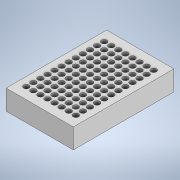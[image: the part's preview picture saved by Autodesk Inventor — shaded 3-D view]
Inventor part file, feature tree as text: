
AUTODESK INVENTOR PART (.ipt)
format: ipt  version: 2020 (Build 240168000, 168)  size: 244,736 bytes
history: native  units: in
note: dims shown in document units (in); Inventor stores cm internally (conversion verified against a paired STEP export)
features: sketch x2, extrude x1, hole x1, pattern_linear x1
ambient origin geometry x8: Origin, YZ Plane, XZ Plane, XY Plane, X Axis, Y Axis, Z Axis, Center Point
bodies: Solid1 (feature_tree)
feature tree (5):
  extrude  "Extrusion1"  Depth=5.03in
  hole  "Hole1"  [1 undecoded]
  pattern_linear  "Rectangular Pattern1"  Spacing1=0.5661in  [1 undecoded]
  sketch  "Sketch1"  dims[d0=3.365in d1=5.03in]
  sketch  "Sketch2"  dims[d2=1.0in d3=0.0in d4=0.4425in d5=0.5661in d6=0.2756in d7=0.2756in d8=0.75in d9=0.37in d10=0.25in d11=90.0deg d12=0.75in d13=0.0in d14=3.1496in d16=0.3543in d17=4.7244in d19=0.3543in]
note: 2 required parameter values undecoded (feature->parameter linkage not recoverable at this tier; creation-order binding heuristic only, values carry confidence <= 0.55)
